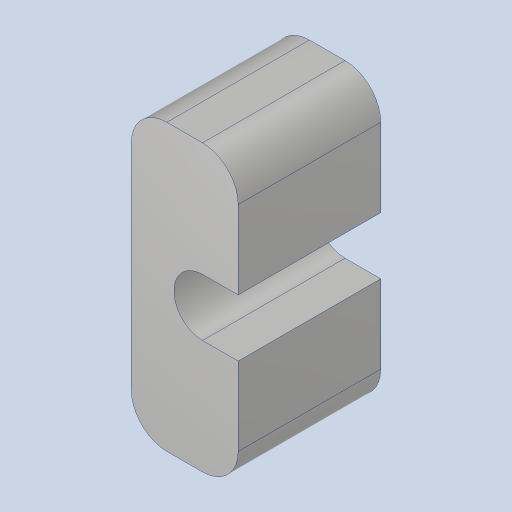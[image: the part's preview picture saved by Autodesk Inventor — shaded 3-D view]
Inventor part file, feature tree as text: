
AUTODESK INVENTOR PART (.ipt)
format: ipt  version: 2023.4 (Build 274418000, 418)  size: 118,784 bytes
history: native  units: in
note: dims shown in document units (in); Inventor stores cm internally (conversion verified against a paired STEP export)
features: extrude x1, fillet x1, sketch x1
ambient origin geometry x8: Origin, YZ Plane, XZ Plane, XY Plane, X Axis, Y Axis, Z Axis, Center Point
bodies: Solid1 (feature_tree)
feature tree (3):
  extrude  "Extrusion1"  Depth=1.0in
  fillet  "Fillet1"  Radius=0.125in
  sketch  "Sketch1"  dims[d0=0.375in d1=1.0in d2=0.125in d3=0.5in d4=0.201in d5=0.5in d6=0.0in d7=0.125in]
